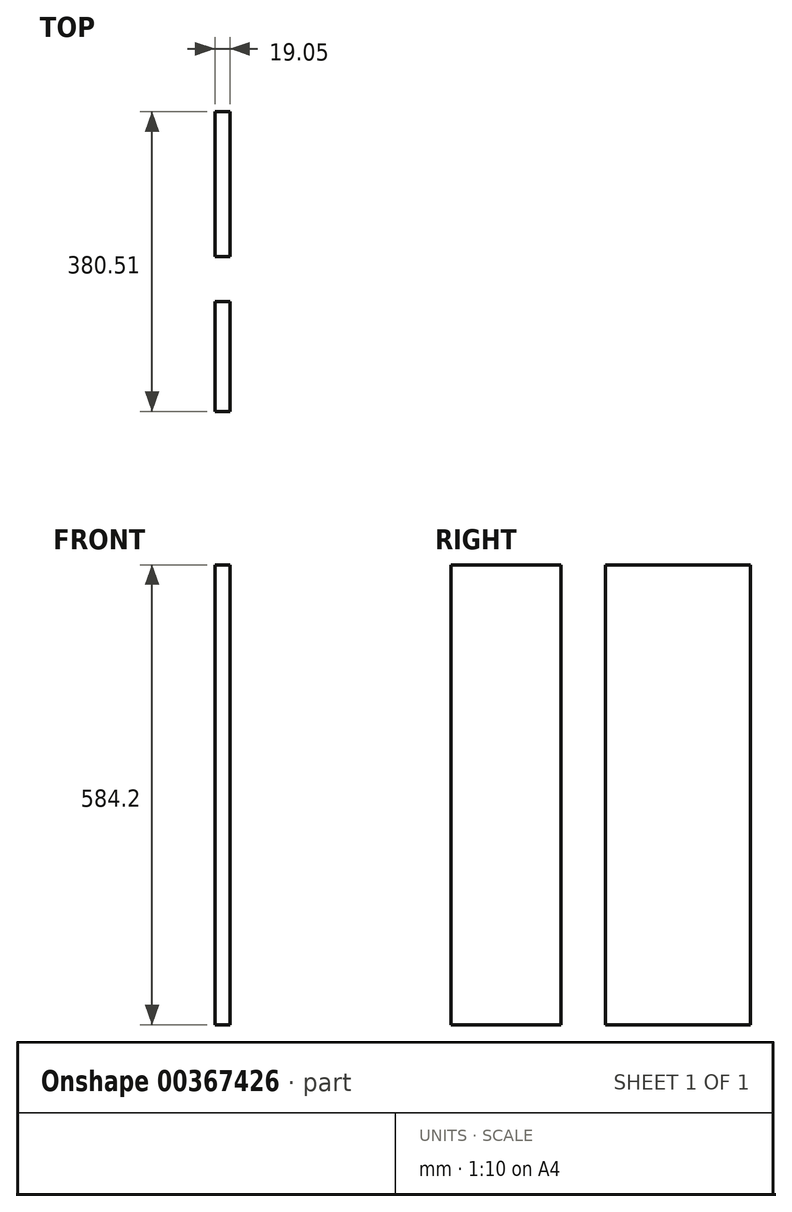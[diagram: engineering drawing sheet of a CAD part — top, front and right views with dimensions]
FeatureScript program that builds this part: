
annotation { "Feature Type Name" : "Feature", "Feature Type Description" : "" }
export const myFeature = defineFeature(function(context is Context, id is Id, definition is map)
    precondition{}
    {
        {
            var Q0;
            Q0=qCreatedBy(makeId("Right.planeOp"),FACE);
            var sketch = newSketch(context, id + "F0", { "sketchPlane" : qUnion([Q0])});
            skLineSegment(sketch, "E0.bottom", {"start": v(92.07, 292.1) * mm, "end": v(-92.08, 292.1) * mm});
            skLineSegment(sketch, "E0.top", {"start": v(92.08, -292.1) * mm, "end": v(-92.07, -292.1) * mm});
            skLineSegment(sketch, "E0.left", {"start": v(92.07, 292.1) * mm, "end": v(92.08, -292.1) * mm});
            skLineSegment(sketch, "E0.right", {"start": v(-92.08, 292.1) * mm, "end": v(-92.07, -292.1) * mm});
            skPoint(sketch, "E0.middle", {"position": v(0, 0) * mm});
            skSolve(sketch);
        }
        {
            var Q0;
            Q0=makeQuery(id+"F0.imprint","IMPRINT",FACE,{"disambiguationData":[TD([[makeQuery(id+"F0.imprint","IMPRINT",EDGE,{"derivedFrom":sQuery(id+"F0.wireOp",EDGE,"E0.bottom")}),1.0]])]});
            extrude(context, id + "F1", {"entities" : qUnion([Q0]), "depth" : 19.05 * mm});
        }
        {
            var Q0;
            Q0=qCreatedBy(makeId("Right.planeOp"),FACE);
            var sketch = newSketch(context, id + "F2", { "sketchPlane" : qUnion([Q0])});
            skLineSegment(sketch, "E1.bottom", {"start": v(-288.43, 292.1) * mm, "end": v(-148.73, 292.1) * mm});
            skLineSegment(sketch, "E1.top", {"start": v(-288.43, -292.1) * mm, "end": v(-148.73, -292.1) * mm});
            skLineSegment(sketch, "E1.left", {"start": v(-288.43, 292.1) * mm, "end": v(-288.43, -292.1) * mm});
            skLineSegment(sketch, "E1.right", {"start": v(-148.73, 292.1) * mm, "end": v(-148.73, -292.1) * mm});
            skPoint(sketch, "E1.middle", {"position": v(-218.58, 0) * mm});
            skSolve(sketch);
        }
        {
            var Q0;
            Q0 = qSketchRegion(id + "F2", true);
            extrude(context, id + "F3", {"entities" : qUnion([Q0]), "depth" : 19.05 * mm});
        }
    });
